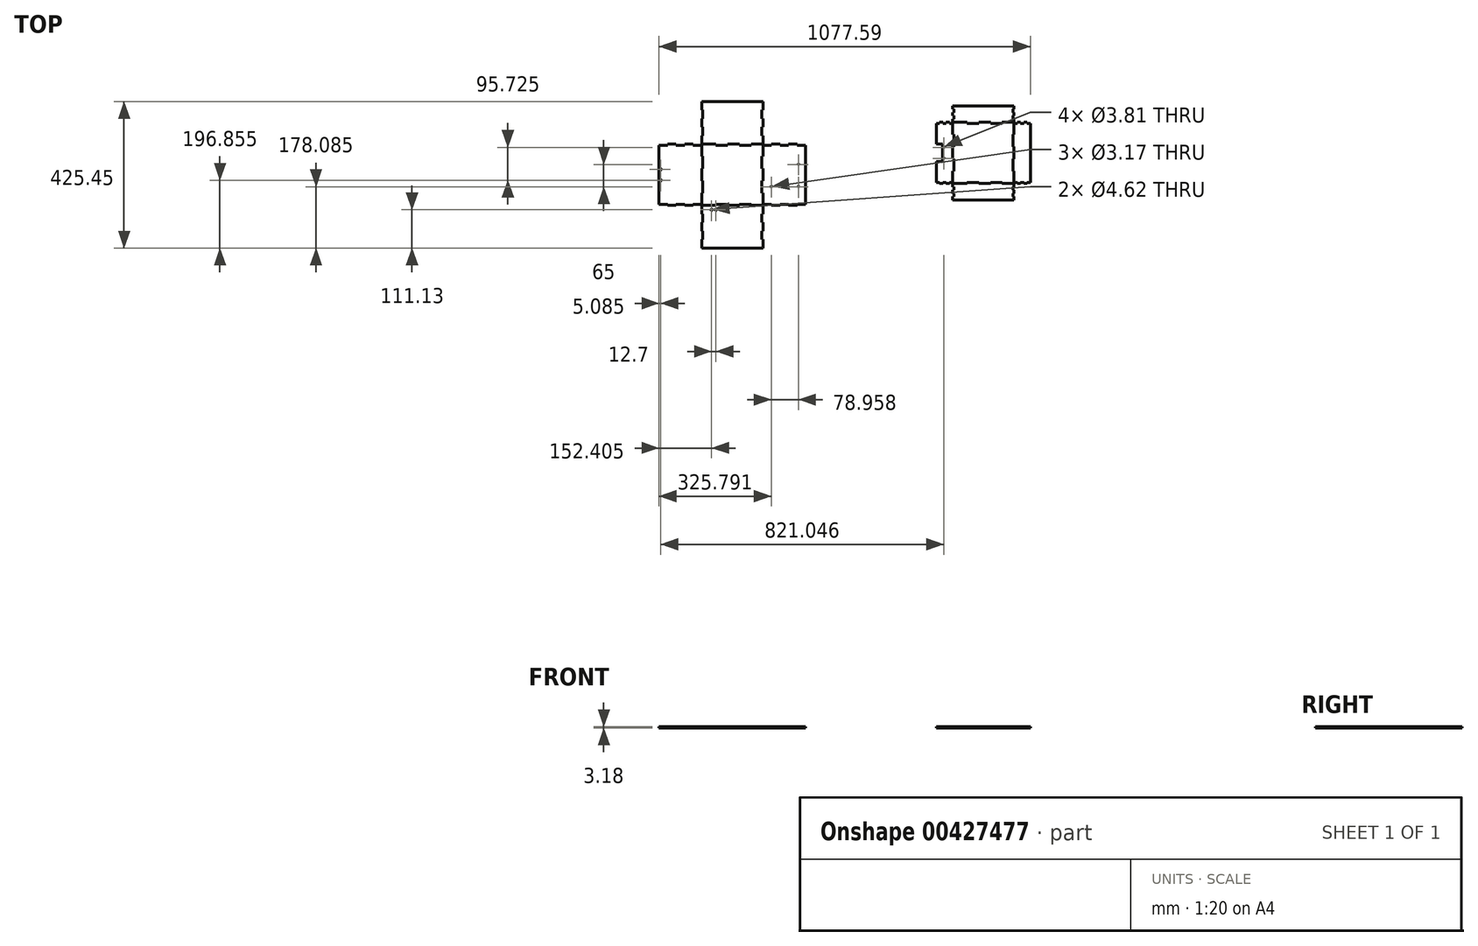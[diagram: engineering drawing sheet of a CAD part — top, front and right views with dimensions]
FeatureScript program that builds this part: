
annotation { "Feature Type Name" : "Feature", "Feature Type Description" : "" }
export const myFeature = defineFeature(function(context is Context, id is Id, definition is map)
    precondition{}
    {
        {
            var Q0;
            Q0=qCreatedBy(makeId("Top.planeOp"),FACE);
            var sketch = newSketch(context, id + "F0", { "sketchPlane" : qUnion([Q0])});
            skLineSegment(sketch, "E0.bottom", {"start": v(0, 0) * mm, "end": v(41.1, 0) * mm});
            skLineSegment(sketch, "E0.top", {"start": v(0, 177.8) * mm, "end": v(41.1, 177.8) * mm});
            skLineSegment(sketch, "E0.left", {"start": v(0, 0) * mm, "end": v(0, 35.56) * mm});
            skLineSegment(sketch, "E0.right", {"start": v(177.8, 0) * mm, "end": v(177.8, 35.56) * mm});
            skLineSegment(sketch, "E1", {"start": v(41.1, 177.8) * mm, "end": v(41.1, 174.62) * mm});
            skLineSegment(sketch, "E2", {"start": v(41.1, 174.62) * mm, "end": v(75.28, 174.62) * mm});
            skLineSegment(sketch, "E3", {"start": v(75.28, 174.62) * mm, "end": v(75.28, 177.8) * mm});
            skLineSegment(sketch, "E4", {"start": v(75.28, 177.8) * mm, "end": v(109.45, 177.8) * mm});
            skLineSegment(sketch, "E5", {"start": v(109.45, 177.8) * mm, "end": v(109.45, 174.62) * mm});
            skLineSegment(sketch, "E6", {"start": v(109.45, 174.62) * mm, "end": v(143.63, 174.62) * mm});
            skLineSegment(sketch, "E7", {"start": v(143.63, 174.62) * mm, "end": v(143.63, 177.8) * mm});
            skLineSegment(sketch, "E8", {"start": v(177.8, 142.24) * mm, "end": v(174.63, 142.24) * mm});
            skLineSegment(sketch, "E9", {"start": v(174.63, 142.24) * mm, "end": v(174.63, 106.68) * mm});
            skLineSegment(sketch, "E10", {"start": v(174.63, 106.68) * mm, "end": v(177.8, 106.68) * mm});
            skLineSegment(sketch, "E11", {"start": v(177.8, 71.12) * mm, "end": v(174.62, 71.12) * mm});
            skLineSegment(sketch, "E12", {"start": v(174.62, 71.12) * mm, "end": v(174.62, 35.56) * mm});
            skLineSegment(sketch, "E13", {"start": v(174.62, 35.56) * mm, "end": v(177.8, 35.56) * mm});
            skLineSegment(sketch, "E14", {"start": v(0, 142.24) * mm, "end": v(3.18, 142.24) * mm});
            skLineSegment(sketch, "E15", {"start": v(3.18, 142.24) * mm, "end": v(3.18, 106.68) * mm});
            skLineSegment(sketch, "E16", {"start": v(3.18, 106.68) * mm, "end": v(0, 106.68) * mm});
            skLineSegment(sketch, "E17", {"start": v(0, 71.12) * mm, "end": v(3.18, 71.12) * mm});
            skLineSegment(sketch, "E18", {"start": v(3.18, 71.12) * mm, "end": v(3.18, 35.56) * mm});
            skLineSegment(sketch, "E19", {"start": v(3.18, 35.56) * mm, "end": v(0, 35.56) * mm});
            skLineSegment(sketch, "E20", {"start": v(41.1, 0) * mm, "end": v(41.1, 3.18) * mm});
            skLineSegment(sketch, "E21", {"start": v(41.1, 3.18) * mm, "end": v(75.28, 3.18) * mm});
            skLineSegment(sketch, "E22", {"start": v(75.28, 3.18) * mm, "end": v(75.28, 0) * mm});
            skLineSegment(sketch, "E23", {"start": v(109.45, 0) * mm, "end": v(109.45, 3.18) * mm});
            skLineSegment(sketch, "E24", {"start": v(109.45, 3.18) * mm, "end": v(143.63, 3.18) * mm});
            skLineSegment(sketch, "E25", {"start": v(143.63, 3.18) * mm, "end": v(143.63, 0) * mm});
            skLineSegment(sketch, "E26.trimOffspring", {"start": v(0, 142.24) * mm, "end": v(0, 177.8) * mm});
            skLineSegment(sketch, "E27.trimOffspring", {"start": v(143.63, 177.8) * mm, "end": v(177.8, 177.8) * mm});
            skLineSegment(sketch, "E28.trimOffspring", {"start": v(177.8, 142.24) * mm, "end": v(177.8, 177.8) * mm});
            skLineSegment(sketch, "E29.trimOffspring", {"start": v(177.8, 71.12) * mm, "end": v(177.8, 106.68) * mm});
            skLineSegment(sketch, "E30.trimOffspring", {"start": v(143.63, 0) * mm, "end": v(177.8, 0) * mm});
            skLineSegment(sketch, "E31.trimOffspring", {"start": v(75.28, 0) * mm, "end": v(109.45, 0) * mm});
            skLineSegment(sketch, "E32.trimOffspring", {"start": v(0, 71.12) * mm, "end": v(0, 106.68) * mm});
            skLineSegment(sketch, "E33", {"start": v(-24.77, 0) * mm, "end": v(-49.53, 0) * mm});
            skLineSegment(sketch, "E34", {"start": v(-123.83, 3.17) * mm, "end": v(-123.83, 174.62) * mm});
            skLineSegment(sketch, "E35", {"start": v(-99.06, 177.8) * mm, "end": v(-74.3, 177.8) * mm});
            skLineSegment(sketch, "E36", {"start": v(0, 301.62) * mm, "end": v(177.8, 301.62) * mm});
            skLineSegment(sketch, "E37", {"start": v(177.8, 301.62) * mm, "end": v(177.8, 276.86) * mm});
            skLineSegment(sketch, "E38", {"start": v(0, 301.62) * mm, "end": v(0, 276.86) * mm});
            skLineSegment(sketch, "E39", {"start": v(202.57, 177.8) * mm, "end": v(227.33, 177.8) * mm});
            skLineSegment(sketch, "E40", {"start": v(301.63, 174.62) * mm, "end": v(301.63, 3.18) * mm});
            skLineSegment(sketch, "E41", {"start": v(276.86, 0) * mm, "end": v(252.1, 0) * mm});
            skLineSegment(sketch, "E42", {"start": v(177.8, 0) * mm, "end": v(177.8, -24.77) * mm});
            skLineSegment(sketch, "E43", {"start": v(177.8, -123.83) * mm, "end": v(0, -123.83) * mm});
            skLineSegment(sketch, "E44", {"start": v(0, -123.83) * mm, "end": v(0, -99.06) * mm});
            skLineSegment(sketch, "E45", {"start": v(0, 276.86) * mm, "end": v(3.18, 276.86) * mm});
            skLineSegment(sketch, "E46", {"start": v(3.18, 276.86) * mm, "end": v(3.18, 252.1) * mm});
            skLineSegment(sketch, "E47", {"start": v(3.18, 252.1) * mm, "end": v(0, 252.1) * mm});
            skLineSegment(sketch, "E48", {"start": v(0, 227.33) * mm, "end": v(3.18, 227.33) * mm});
            skLineSegment(sketch, "E49", {"start": v(3.18, 227.33) * mm, "end": v(3.18, 202.56) * mm});
            skLineSegment(sketch, "E50", {"start": v(3.18, 202.56) * mm, "end": v(0, 202.56) * mm});
            skLineSegment(sketch, "E51", {"start": v(177.8, 276.86) * mm, "end": v(174.62, 276.86) * mm});
            skLineSegment(sketch, "E52", {"start": v(174.62, 276.86) * mm, "end": v(174.62, 252.1) * mm});
            skLineSegment(sketch, "E53", {"start": v(174.62, 252.1) * mm, "end": v(177.8, 252.1) * mm});
            skLineSegment(sketch, "E54", {"start": v(177.8, 227.33) * mm, "end": v(174.62, 227.33) * mm});
            skLineSegment(sketch, "E55", {"start": v(174.62, 227.33) * mm, "end": v(174.62, 202.56) * mm});
            skLineSegment(sketch, "E56", {"start": v(174.62, 202.56) * mm, "end": v(177.8, 202.56) * mm});
            skLineSegment(sketch, "E57.trimOffspring", {"start": v(0, 252.1) * mm, "end": v(0, 227.33) * mm});
            skLineSegment(sketch, "E58.trimOffspring", {"start": v(0, 202.56) * mm, "end": v(0, 177.8) * mm});
            skLineSegment(sketch, "E59.trimOffspring", {"start": v(177.8, 252.1) * mm, "end": v(177.8, 227.33) * mm});
            skLineSegment(sketch, "E60.trimOffspring", {"start": v(177.8, 202.56) * mm, "end": v(177.8, 177.8) * mm});
            skLineSegment(sketch, "E61", {"start": v(0, -24.77) * mm, "end": v(3.18, -24.77) * mm});
            skLineSegment(sketch, "E62", {"start": v(3.18, -24.77) * mm, "end": v(3.18, -49.53) * mm});
            skLineSegment(sketch, "E63", {"start": v(3.18, -49.53) * mm, "end": v(0, -49.53) * mm});
            skLineSegment(sketch, "E64", {"start": v(0, -74.3) * mm, "end": v(3.18, -74.3) * mm});
            skLineSegment(sketch, "E65", {"start": v(3.18, -74.3) * mm, "end": v(3.18, -99.06) * mm});
            skLineSegment(sketch, "E66", {"start": v(3.18, -99.06) * mm, "end": v(0, -99.06) * mm});
            skLineSegment(sketch, "E67", {"start": v(177.8, -24.77) * mm, "end": v(174.63, -24.77) * mm});
            skLineSegment(sketch, "E68", {"start": v(174.63, -24.77) * mm, "end": v(174.63, -49.53) * mm});
            skLineSegment(sketch, "E69", {"start": v(174.63, -49.53) * mm, "end": v(177.8, -49.53) * mm});
            skLineSegment(sketch, "E70", {"start": v(177.8, -74.3) * mm, "end": v(174.63, -74.3) * mm});
            skLineSegment(sketch, "E71", {"start": v(174.63, -74.3) * mm, "end": v(174.63, -99.06) * mm});
            skLineSegment(sketch, "E72", {"start": v(174.63, -99.06) * mm, "end": v(177.8, -99.06) * mm});
            skLineSegment(sketch, "E73.trimOffspring", {"start": v(0, -24.77) * mm, "end": v(0, 0) * mm});
            skLineSegment(sketch, "E74.trimOffspring", {"start": v(0, -74.3) * mm, "end": v(0, -49.53) * mm});
            skLineSegment(sketch, "E75.trimOffspring", {"start": v(177.8, -49.53) * mm, "end": v(177.8, -74.3) * mm});
            skLineSegment(sketch, "E76.trimOffspring", {"start": v(177.8, -99.06) * mm, "end": v(177.8, -123.83) * mm});
            skLineSegment(sketch, "E77", {"start": v(177.8, 174.62) * mm, "end": v(202.57, 174.62) * mm});
            skLineSegment(sketch, "E78", {"start": v(202.57, 174.62) * mm, "end": v(202.57, 177.8) * mm});
            skLineSegment(sketch, "E79", {"start": v(227.33, 177.8) * mm, "end": v(227.33, 174.62) * mm});
            skLineSegment(sketch, "E80", {"start": v(227.33, 174.62) * mm, "end": v(252.1, 174.62) * mm});
            skLineSegment(sketch, "E81", {"start": v(252.1, 174.63) * mm, "end": v(252.1, 177.8) * mm});
            skLineSegment(sketch, "E82", {"start": v(276.86, 177.8) * mm, "end": v(276.86, 174.62) * mm});
            skLineSegment(sketch, "E83", {"start": v(276.86, 174.62) * mm, "end": v(301.62, 174.62) * mm});
            skLineSegment(sketch, "E84", {"start": v(177.8, 3.18) * mm, "end": v(202.57, 3.18) * mm});
            skLineSegment(sketch, "E85", {"start": v(202.57, 3.18) * mm, "end": v(202.57, 0) * mm});
            skLineSegment(sketch, "E86", {"start": v(276.86, 0) * mm, "end": v(276.86, 3.18) * mm});
            skLineSegment(sketch, "E87", {"start": v(276.86, 3.18) * mm, "end": v(301.63, 3.18) * mm});
            skLineSegment(sketch, "E88", {"start": v(227.33, 0) * mm, "end": v(227.33, 3.18) * mm});
            skLineSegment(sketch, "E89", {"start": v(227.33, 3.18) * mm, "end": v(252.1, 3.18) * mm});
            skLineSegment(sketch, "E90", {"start": v(252.1, 3.18) * mm, "end": v(252.1, 0) * mm});
            skLineSegment(sketch, "E91.trimOffspring", {"start": v(252.1, 177.8) * mm, "end": v(276.86, 177.8) * mm});
            skPoint(sketch, "E92.orphan", {"position": v(301.63, 0) * mm});
            skLineSegment(sketch, "E93.trimOffspring", {"start": v(227.33, 0) * mm, "end": v(202.57, 0) * mm});
            skLineSegment(sketch, "E94", {"start": v(0, 174.62) * mm, "end": v(-24.77, 174.62) * mm});
            skLineSegment(sketch, "E95", {"start": v(-24.77, 174.62) * mm, "end": v(-24.77, 177.8) * mm});
            skLineSegment(sketch, "E96", {"start": v(-123.83, 174.62) * mm, "end": v(-99.06, 174.62) * mm});
            skLineSegment(sketch, "E97", {"start": v(-99.06, 174.62) * mm, "end": v(-99.06, 177.8) * mm});
            skLineSegment(sketch, "E98", {"start": v(-74.3, 177.8) * mm, "end": v(-74.3, 174.62) * mm});
            skLineSegment(sketch, "E99", {"start": v(-74.3, 174.62) * mm, "end": v(-49.53, 174.62) * mm});
            skLineSegment(sketch, "E100", {"start": v(-49.53, 174.62) * mm, "end": v(-49.53, 177.8) * mm});
            skLineSegment(sketch, "E101", {"start": v(0, 3.18) * mm, "end": v(-24.77, 3.18) * mm});
            skLineSegment(sketch, "E102", {"start": v(-24.77, 3.18) * mm, "end": v(-24.77, 0) * mm});
            skLineSegment(sketch, "E103", {"start": v(-99.06, 0) * mm, "end": v(-99.06, 3.18) * mm});
            skLineSegment(sketch, "E104", {"start": v(-99.06, 3.18) * mm, "end": v(-123.83, 3.18) * mm});
            skLineSegment(sketch, "E105", {"start": v(-74.3, 0) * mm, "end": v(-74.3, 3.18) * mm});
            skLineSegment(sketch, "E106", {"start": v(-74.3, 3.18) * mm, "end": v(-49.53, 3.18) * mm});
            skLineSegment(sketch, "E107", {"start": v(-49.53, 3.18) * mm, "end": v(-49.53, 0) * mm});
            skLineSegment(sketch, "E108.trimOffspring", {"start": v(-49.53, 177.8) * mm, "end": v(-24.77, 177.8) * mm});
            skLineSegment(sketch, "E109.trimOffspring", {"start": v(-74.3, 0) * mm, "end": v(-99.06, 0) * mm});
            skLineSegment(sketch, "E110.bottom", {"start": v(728.34, 63.97) * mm, "end": v(769.44, 63.97) * mm});
            skLineSegment(sketch, "E110.top", {"start": v(728.34, 241.77) * mm, "end": v(769.44, 241.77) * mm});
            skLineSegment(sketch, "E110.left", {"start": v(728.34, 63.97) * mm, "end": v(728.34, 99.53) * mm});
            skLineSegment(sketch, "E110.right", {"start": v(906.14, 63.97) * mm, "end": v(906.14, 99.53) * mm});
            skLineSegment(sketch, "E111", {"start": v(769.44, 241.77) * mm, "end": v(769.44, 238.6) * mm});
            skLineSegment(sketch, "E112", {"start": v(769.44, 238.6) * mm, "end": v(803.61, 238.6) * mm});
            skLineSegment(sketch, "E113", {"start": v(803.61, 238.6) * mm, "end": v(803.61, 241.77) * mm});
            skLineSegment(sketch, "E114", {"start": v(803.61, 241.77) * mm, "end": v(837.79, 241.77) * mm});
            skLineSegment(sketch, "E115", {"start": v(837.79, 241.77) * mm, "end": v(837.79, 238.6) * mm});
            skLineSegment(sketch, "E116", {"start": v(837.79, 238.6) * mm, "end": v(871.96, 238.6) * mm});
            skLineSegment(sketch, "E117", {"start": v(871.96, 238.6) * mm, "end": v(871.96, 241.77) * mm});
            skLineSegment(sketch, "E118", {"start": v(906.14, 206.21) * mm, "end": v(902.96, 206.21) * mm});
            skLineSegment(sketch, "E119", {"start": v(902.96, 206.21) * mm, "end": v(902.96, 170.65) * mm});
            skLineSegment(sketch, "E120", {"start": v(902.96, 170.65) * mm, "end": v(906.14, 170.65) * mm});
            skLineSegment(sketch, "E121", {"start": v(906.14, 135.1) * mm, "end": v(902.96, 135.1) * mm});
            skLineSegment(sketch, "E122", {"start": v(902.96, 135.1) * mm, "end": v(902.96, 99.53) * mm});
            skLineSegment(sketch, "E123", {"start": v(902.96, 99.53) * mm, "end": v(906.14, 99.53) * mm});
            skLineSegment(sketch, "E124", {"start": v(728.34, 206.21) * mm, "end": v(731.51, 206.21) * mm});
            skLineSegment(sketch, "E125", {"start": v(731.51, 206.21) * mm, "end": v(731.51, 170.65) * mm});
            skLineSegment(sketch, "E126", {"start": v(731.51, 170.65) * mm, "end": v(728.34, 170.65) * mm});
            skLineSegment(sketch, "E127", {"start": v(728.34, 135.1) * mm, "end": v(731.51, 135.1) * mm});
            skLineSegment(sketch, "E128", {"start": v(731.51, 135.1) * mm, "end": v(731.51, 99.53) * mm});
            skLineSegment(sketch, "E129", {"start": v(731.51, 99.53) * mm, "end": v(728.34, 99.53) * mm});
            skLineSegment(sketch, "E130", {"start": v(769.44, 63.97) * mm, "end": v(769.44, 67.15) * mm});
            skLineSegment(sketch, "E131", {"start": v(769.44, 67.15) * mm, "end": v(803.61, 67.15) * mm});
            skLineSegment(sketch, "E132", {"start": v(803.61, 67.15) * mm, "end": v(803.61, 63.97) * mm});
            skLineSegment(sketch, "E133", {"start": v(837.79, 63.97) * mm, "end": v(837.79, 67.15) * mm});
            skLineSegment(sketch, "E134", {"start": v(837.79, 67.15) * mm, "end": v(871.96, 67.15) * mm});
            skLineSegment(sketch, "E135", {"start": v(871.96, 67.15) * mm, "end": v(871.96, 63.97) * mm});
            skLineSegment(sketch, "E136.trimOffspring", {"start": v(728.34, 206.21) * mm, "end": v(728.34, 241.77) * mm});
            skLineSegment(sketch, "E137.trimOffspring", {"start": v(871.96, 241.77) * mm, "end": v(906.14, 241.77) * mm});
            skLineSegment(sketch, "E138.trimOffspring", {"start": v(906.14, 206.21) * mm, "end": v(906.14, 241.77) * mm});
            skLineSegment(sketch, "E139.trimOffspring", {"start": v(906.14, 135.1) * mm, "end": v(906.14, 170.65) * mm});
            skLineSegment(sketch, "E140.trimOffspring", {"start": v(871.96, 63.97) * mm, "end": v(906.14, 63.97) * mm});
            skLineSegment(sketch, "E141.trimOffspring", {"start": v(803.61, 63.97) * mm, "end": v(837.79, 63.97) * mm});
            skLineSegment(sketch, "E142.trimOffspring", {"start": v(728.34, 135.1) * mm, "end": v(728.34, 170.65) * mm});
            skLineSegment(sketch, "E143", {"start": v(718.81, 63.97) * mm, "end": v(709.29, 63.97) * mm});
            skLineSegment(sketch, "E144", {"start": v(680.71, 67.15) * mm, "end": v(680.71, 238.6) * mm});
            skLineSegment(sketch, "E145", {"start": v(690.24, 241.77) * mm, "end": v(699.76, 241.77) * mm});
            skLineSegment(sketch, "E146", {"start": v(728.34, 289.4) * mm, "end": v(906.14, 289.4) * mm});
            skLineSegment(sketch, "E147", {"start": v(906.14, 289.4) * mm, "end": v(906.14, 279.87) * mm});
            skLineSegment(sketch, "E148", {"start": v(728.34, 289.4) * mm, "end": v(728.34, 279.87) * mm});
            skLineSegment(sketch, "E149", {"start": v(915.66, 241.77) * mm, "end": v(925.19, 241.77) * mm});
            skLineSegment(sketch, "E150", {"start": v(953.76, 238.6) * mm, "end": v(953.76, 67.15) * mm});
            skLineSegment(sketch, "E151", {"start": v(944.24, 63.97) * mm, "end": v(934.71, 63.97) * mm});
            skLineSegment(sketch, "E152", {"start": v(906.14, 63.97) * mm, "end": v(906.14, 54.45) * mm});
            skLineSegment(sketch, "E153", {"start": v(906.14, 16.35) * mm, "end": v(728.34, 16.35) * mm});
            skLineSegment(sketch, "E154", {"start": v(728.34, 16.35) * mm, "end": v(728.34, 25.87) * mm});
            skLineSegment(sketch, "E155", {"start": v(728.34, 279.87) * mm, "end": v(731.51, 279.87) * mm});
            skLineSegment(sketch, "E156", {"start": v(731.51, 279.87) * mm, "end": v(731.51, 270.35) * mm});
            skLineSegment(sketch, "E157", {"start": v(731.51, 270.35) * mm, "end": v(728.34, 270.35) * mm});
            skLineSegment(sketch, "E158", {"start": v(728.34, 260.82) * mm, "end": v(731.51, 260.82) * mm});
            skLineSegment(sketch, "E159", {"start": v(731.51, 260.82) * mm, "end": v(731.51, 251.3) * mm});
            skLineSegment(sketch, "E160", {"start": v(731.51, 251.3) * mm, "end": v(728.34, 251.3) * mm});
            skLineSegment(sketch, "E161", {"start": v(906.14, 279.87) * mm, "end": v(902.96, 279.87) * mm});
            skLineSegment(sketch, "E162", {"start": v(902.96, 279.87) * mm, "end": v(902.96, 270.35) * mm});
            skLineSegment(sketch, "E163", {"start": v(902.96, 270.35) * mm, "end": v(906.14, 270.35) * mm});
            skLineSegment(sketch, "E164", {"start": v(906.14, 260.82) * mm, "end": v(902.96, 260.82) * mm});
            skLineSegment(sketch, "E165", {"start": v(902.96, 260.82) * mm, "end": v(902.96, 251.3) * mm});
            skLineSegment(sketch, "E166", {"start": v(902.96, 251.3) * mm, "end": v(906.14, 251.3) * mm});
            skLineSegment(sketch, "E167.trimOffspring", {"start": v(728.34, 270.35) * mm, "end": v(728.34, 260.82) * mm});
            skLineSegment(sketch, "E168.trimOffspring", {"start": v(728.34, 251.3) * mm, "end": v(728.34, 241.77) * mm});
            skLineSegment(sketch, "E169.trimOffspring", {"start": v(906.14, 270.35) * mm, "end": v(906.14, 260.82) * mm});
            skLineSegment(sketch, "E170.trimOffspring", {"start": v(906.14, 251.3) * mm, "end": v(906.14, 241.77) * mm});
            skLineSegment(sketch, "E171", {"start": v(728.34, 54.45) * mm, "end": v(731.51, 54.45) * mm});
            skLineSegment(sketch, "E172", {"start": v(731.51, 54.45) * mm, "end": v(731.51, 44.92) * mm});
            skLineSegment(sketch, "E173", {"start": v(731.51, 44.92) * mm, "end": v(728.34, 44.92) * mm});
            skLineSegment(sketch, "E174", {"start": v(728.34, 35.4) * mm, "end": v(731.51, 35.4) * mm});
            skLineSegment(sketch, "E175", {"start": v(731.51, 35.4) * mm, "end": v(731.51, 25.87) * mm});
            skLineSegment(sketch, "E176", {"start": v(731.51, 25.87) * mm, "end": v(728.34, 25.87) * mm});
            skLineSegment(sketch, "E177", {"start": v(906.14, 54.45) * mm, "end": v(902.96, 54.45) * mm});
            skLineSegment(sketch, "E178", {"start": v(902.96, 54.45) * mm, "end": v(902.96, 44.92) * mm});
            skLineSegment(sketch, "E179", {"start": v(902.96, 44.92) * mm, "end": v(906.14, 44.92) * mm});
            skLineSegment(sketch, "E180", {"start": v(906.14, 35.4) * mm, "end": v(902.96, 35.4) * mm});
            skLineSegment(sketch, "E181", {"start": v(902.96, 35.4) * mm, "end": v(902.96, 25.87) * mm});
            skLineSegment(sketch, "E182", {"start": v(902.96, 25.87) * mm, "end": v(906.14, 25.87) * mm});
            skLineSegment(sketch, "E183.trimOffspring", {"start": v(728.34, 54.45) * mm, "end": v(728.34, 63.97) * mm});
            skLineSegment(sketch, "E184.trimOffspring", {"start": v(728.34, 35.4) * mm, "end": v(728.34, 44.92) * mm});
            skLineSegment(sketch, "E185.trimOffspring", {"start": v(906.14, 44.92) * mm, "end": v(906.14, 35.4) * mm});
            skLineSegment(sketch, "E186.trimOffspring", {"start": v(906.14, 25.87) * mm, "end": v(906.14, 16.35) * mm});
            skLineSegment(sketch, "E187", {"start": v(906.14, 238.6) * mm, "end": v(915.66, 238.6) * mm});
            skLineSegment(sketch, "E188", {"start": v(915.66, 238.6) * mm, "end": v(915.66, 241.77) * mm});
            skLineSegment(sketch, "E189", {"start": v(925.19, 241.77) * mm, "end": v(925.19, 238.6) * mm});
            skLineSegment(sketch, "E190", {"start": v(925.19, 238.6) * mm, "end": v(934.71, 238.6) * mm});
            skLineSegment(sketch, "E191", {"start": v(934.71, 238.6) * mm, "end": v(934.71, 241.77) * mm});
            skLineSegment(sketch, "E192", {"start": v(944.24, 241.77) * mm, "end": v(944.24, 238.6) * mm});
            skLineSegment(sketch, "E193", {"start": v(944.24, 238.6) * mm, "end": v(953.76, 238.6) * mm});
            skLineSegment(sketch, "E194", {"start": v(906.14, 67.15) * mm, "end": v(915.66, 67.15) * mm});
            skLineSegment(sketch, "E195", {"start": v(915.66, 67.15) * mm, "end": v(915.66, 63.97) * mm});
            skLineSegment(sketch, "E196", {"start": v(944.24, 63.97) * mm, "end": v(944.24, 67.15) * mm});
            skLineSegment(sketch, "E197", {"start": v(944.24, 67.15) * mm, "end": v(953.76, 67.15) * mm});
            skLineSegment(sketch, "E198", {"start": v(925.19, 63.97) * mm, "end": v(925.19, 67.15) * mm});
            skLineSegment(sketch, "E199", {"start": v(925.19, 67.15) * mm, "end": v(934.71, 67.15) * mm});
            skLineSegment(sketch, "E200", {"start": v(934.71, 67.15) * mm, "end": v(934.71, 63.97) * mm});
            skLineSegment(sketch, "E201.trimOffspring", {"start": v(934.71, 241.77) * mm, "end": v(944.24, 241.77) * mm});
            skPoint(sketch, "E202.orphan", {"position": v(953.76, 63.97) * mm});
            skLineSegment(sketch, "E203.trimOffspring", {"start": v(925.19, 63.97) * mm, "end": v(915.66, 63.97) * mm});
            skLineSegment(sketch, "E204", {"start": v(728.34, 238.6) * mm, "end": v(718.81, 238.6) * mm});
            skLineSegment(sketch, "E205", {"start": v(718.81, 238.6) * mm, "end": v(718.81, 241.77) * mm});
            skLineSegment(sketch, "E206", {"start": v(680.71, 238.6) * mm, "end": v(690.24, 238.6) * mm});
            skLineSegment(sketch, "E207", {"start": v(690.24, 238.6) * mm, "end": v(690.24, 241.77) * mm});
            skLineSegment(sketch, "E208", {"start": v(699.76, 241.77) * mm, "end": v(699.76, 238.6) * mm});
            skLineSegment(sketch, "E209", {"start": v(699.76, 238.6) * mm, "end": v(709.29, 238.6) * mm});
            skLineSegment(sketch, "E210", {"start": v(709.29, 238.6) * mm, "end": v(709.29, 241.77) * mm});
            skLineSegment(sketch, "E211", {"start": v(728.34, 67.15) * mm, "end": v(718.81, 67.15) * mm});
            skLineSegment(sketch, "E212", {"start": v(718.81, 67.15) * mm, "end": v(718.81, 63.97) * mm});
            skLineSegment(sketch, "E213", {"start": v(690.24, 63.97) * mm, "end": v(690.24, 67.15) * mm});
            skLineSegment(sketch, "E214", {"start": v(690.24, 67.15) * mm, "end": v(680.71, 67.15) * mm});
            skLineSegment(sketch, "E215", {"start": v(699.76, 63.97) * mm, "end": v(699.76, 67.15) * mm});
            skLineSegment(sketch, "E216", {"start": v(699.76, 67.15) * mm, "end": v(709.29, 67.15) * mm});
            skLineSegment(sketch, "E217", {"start": v(709.29, 67.15) * mm, "end": v(709.29, 63.97) * mm});
            skLineSegment(sketch, "E218.trimOffspring", {"start": v(709.29, 241.77) * mm, "end": v(718.81, 241.77) * mm});
            skLineSegment(sketch, "E219.trimOffspring", {"start": v(699.76, 63.97) * mm, "end": v(690.24, 63.97) * mm});
            skSolve(sketch);
        }
        {
            var Q0;
            {var subQ6=sQuery(id+"F0.wireOp",EDGE,"E0.bottom");Q0=makeQuery(id+"F0.imprint","IMPRINT",FACE,{"disambiguationData":[TD([[makeQuery(id+"F0.imprint","IMPRINT",EDGE,{"derivedFrom":subQ6}),1.0]])]});}
            extrude(context, id + "F1", {"entities" : qUnion([Q0]), "depth" : 3.17 * mm});
        }
        {
            var Q0;
            Q0=makeQuery(id+"F0.imprint","IMPRINT",FACE,{"disambiguationData":[TD([[makeQuery(id+"F0.imprint","IMPRINT",EDGE,{"derivedFrom":sQuery(id+"F0.wireOp",EDGE,"E0.top")}),1.0]])]});
            extrude(context, id + "F2", {"entities" : qUnion([Q0]), "depth" : 3.17 * mm});
        }
        {
            var Q0;
            {var subQ3=sQuery(id+"F0.wireOp",EDGE,"E14");Q0=makeQuery(id+"F0.imprint","IMPRINT",FACE,{"disambiguationData":[TD([[makeQuery(id+"F0.imprint","IMPRINT",EDGE,{"derivedFrom":subQ3}),-1.0]])]});}
            extrude(context, id + "F3", {"entities" : qUnion([Q0]), "depth" : 3.17 * mm});
        }
        {
            var Q0;
            {var subQ1=sQuery(id+"F0.wireOp",EDGE,"E8");Q0=makeQuery(id+"F0.imprint","IMPRINT",FACE,{"disambiguationData":[TD([[makeQuery(id+"F0.imprint","IMPRINT",EDGE,{"derivedFrom":subQ1}),1.0]])]});}
            extrude(context, id + "F4", {"entities" : qUnion([Q0]), "depth" : 3.17 * mm});
        }
        {
            var Q0;
            Q0=makeQuery(id+"F0.imprint","IMPRINT",FACE,{"disambiguationData":[TD([[makeQuery(id+"F0.imprint","IMPRINT",EDGE,{"derivedFrom":sQuery(id+"F0.wireOp",EDGE,"E0.bottom")}),-1.0]])]});
            extrude(context, id + "F5", {"entities" : qUnion([Q0]), "depth" : 3.17 * mm});
        }
        {
            var Q0;
            Q0=makeQuery(id+"F5.opExtrude","CAP_FACE",FACE,{"disambiguationData":[OSD([sQuery(id+"F0.wireOp",EDGE,"E0.bottom"),sQuery(id+"F0.wireOp",EDGE,"E20"),sQuery(id+"F0.wireOp",EDGE,"E21"),sQuery(id+"F0.wireOp",EDGE,"E22"),sQuery(id+"F0.wireOp",EDGE,"E23"),sQuery(id+"F0.wireOp",EDGE,"E24"),sQuery(id+"F0.wireOp",EDGE,"E25"),sQuery(id+"F0.wireOp",EDGE,"E30.trimOffspring"),sQuery(id+"F0.wireOp",EDGE,"E31.trimOffspring"),sQuery(id+"F0.wireOp",EDGE,"E42"),sQuery(id+"F0.wireOp",EDGE,"E43"),sQuery(id+"F0.wireOp",EDGE,"E44"),sQuery(id+"F0.wireOp",EDGE,"E61"),sQuery(id+"F0.wireOp",EDGE,"E62"),sQuery(id+"F0.wireOp",EDGE,"E63"),sQuery(id+"F0.wireOp",EDGE,"E64"),sQuery(id+"F0.wireOp",EDGE,"E65"),sQuery(id+"F0.wireOp",EDGE,"E66"),sQuery(id+"F0.wireOp",EDGE,"E67"),sQuery(id+"F0.wireOp",EDGE,"E68"),sQuery(id+"F0.wireOp",EDGE,"E69"),sQuery(id+"F0.wireOp",EDGE,"E70"),sQuery(id+"F0.wireOp",EDGE,"E71"),sQuery(id+"F0.wireOp",EDGE,"E72"),sQuery(id+"F0.wireOp",EDGE,"E73.trimOffspring"),sQuery(id+"F0.wireOp",EDGE,"E74.trimOffspring"),sQuery(id+"F0.wireOp",EDGE,"E75.trimOffspring"),sQuery(id+"F0.wireOp",EDGE,"E76.trimOffspring")])],"isStart":false});
            var sketch = newSketch(context, id + "F6", { "sketchPlane" : qUnion([Q0])});
            skCircle(sketch, "E220", {"center": v(28.57, -12.7) * mm, "radius": 2.31 * mm});
            skCircle(sketch, "E221", {"center": v(41.28, -12.7) * mm, "radius": 2.31 * mm});
            skLineSegment(sketch, "E222.bottom", {"start": v(441.77, 26.41) * mm, "end": v(532.02, 26.41) * mm});
            skLineSegment(sketch, "E222.top", {"start": v(441.77, -58.39) * mm, "end": v(532.02, -58.39) * mm});
            skLineSegment(sketch, "E222.left", {"start": v(441.77, 26.41) * mm, "end": v(441.77, -58.39) * mm});
            skLineSegment(sketch, "E222.right", {"start": v(532.02, 26.41) * mm, "end": v(532.02, -58.39) * mm});
            skPoint(sketch, "E223", {"position": v(486.9, 26.41) * mm});
            skCircle(sketch, "E224", {"center": v(526.82, 14.37) * mm, "radius": 1.59 * mm});
            skCircle(sketch, "E225", {"center": v(526.82, -50.63) * mm, "radius": 1.59 * mm});
            skPoint(sketch, "E226", {"position": v(532.02, -15.99) * mm});
            skCircle(sketch, "E227", {"center": v(447.86, -50.5) * mm, "radius": 1.59 * mm});
            skSolve(sketch);
        }
        {
            var Q0;
            Q0=makeQuery(id+"F6.imprint","IMPRINT",FACE,{"disambiguationData":[TD([[makeQuery(id+"F6.imprint","IMPRINT",EDGE,{"derivedFrom":sQuery(id+"F6.wireOp",EDGE,"E220")}),1.0]])]});
            var Q1;
            Q1=makeQuery(id+"F6.imprint","IMPRINT",FACE,{"disambiguationData":[TD([[makeQuery(id+"F6.imprint","IMPRINT",EDGE,{"derivedFrom":sQuery(id+"F6.wireOp",EDGE,"E221")}),1.0]])]});
            extrude(context, id + "F7", {"entities" : qUnion([Q0, Q1]), "operationType" : NewBodyOperationType.REMOVE, "oppositeDirection" : true, "depth" : 25.4 * mm});
        }
        {
            var Q0;
            Q0=makeQuery(id+"F4.opExtrude","CAP_FACE",FACE,{"disambiguationData":[OSD([sQuery(id+"F0.wireOp",EDGE,"E0.right"),sQuery(id+"F0.wireOp",EDGE,"E8"),sQuery(id+"F0.wireOp",EDGE,"E9"),sQuery(id+"F0.wireOp",EDGE,"E10"),sQuery(id+"F0.wireOp",EDGE,"E11"),sQuery(id+"F0.wireOp",EDGE,"E12"),sQuery(id+"F0.wireOp",EDGE,"E13"),sQuery(id+"F0.wireOp",EDGE,"E28.trimOffspring"),sQuery(id+"F0.wireOp",EDGE,"E29.trimOffspring"),sQuery(id+"F0.wireOp",EDGE,"E39"),sQuery(id+"F0.wireOp",EDGE,"E40"),sQuery(id+"F0.wireOp",EDGE,"E41"),sQuery(id+"F0.wireOp",EDGE,"E77"),sQuery(id+"F0.wireOp",EDGE,"E78"),sQuery(id+"F0.wireOp",EDGE,"E79"),sQuery(id+"F0.wireOp",EDGE,"E80"),sQuery(id+"F0.wireOp",EDGE,"E81"),sQuery(id+"F0.wireOp",EDGE,"E82"),sQuery(id+"F0.wireOp",EDGE,"E83"),sQuery(id+"F0.wireOp",EDGE,"E84"),sQuery(id+"F0.wireOp",EDGE,"E85"),sQuery(id+"F0.wireOp",EDGE,"E86"),sQuery(id+"F0.wireOp",EDGE,"E87"),sQuery(id+"F0.wireOp",EDGE,"E88"),sQuery(id+"F0.wireOp",EDGE,"E89"),sQuery(id+"F0.wireOp",EDGE,"E90"),sQuery(id+"F0.wireOp",EDGE,"E91.trimOffspring"),sQuery(id+"F0.wireOp",EDGE,"E93.trimOffspring")])],"isStart":false});
            var sketch = newSketch(context, id + "F8", { "sketchPlane" : qUnion([Q0])});
            skLineSegment(sketch, "E228.bottom", {"start": v(195.87, 131.3) * mm, "end": v(286.12, 131.3) * mm});
            skLineSegment(sketch, "E228.top", {"start": v(195.87, 46.5) * mm, "end": v(286.12, 46.5) * mm});
            skLineSegment(sketch, "E228.left", {"start": v(195.87, 131.3) * mm, "end": v(195.87, 46.5) * mm});
            skLineSegment(sketch, "E228.right", {"start": v(286.12, 131.3) * mm, "end": v(286.12, 46.5) * mm});
            skPoint(sketch, "E229", {"position": v(241, 131.3) * mm});
            skCircle(sketch, "E230", {"center": v(280.92, 119.25) * mm, "radius": 1.59 * mm});
            skCircle(sketch, "E231", {"center": v(280.92, 54.25) * mm, "radius": 1.59 * mm});
            skPoint(sketch, "E232", {"position": v(286.12, 88.9) * mm});
            skCircle(sketch, "E233", {"center": v(201.96, 54.39) * mm, "radius": 1.59 * mm});
            skPoint(sketch, "E234", {"position": v(301.63, 88.9) * mm});
            skPoint(sketch, "E235", {"position": v(239.71, 174.62) * mm});
            skSolve(sketch);
        }
        {
            var Q0;
            Q0=makeQuery(id+"F8.imprint","IMPRINT",FACE,{"disambiguationData":[TD([[makeQuery(id+"F8.imprint","IMPRINT",EDGE,{"derivedFrom":sQuery(id+"F8.wireOp",EDGE,"E233")}),1.0]])]});
            var Q1;
            Q1=makeQuery(id+"F8.imprint","IMPRINT",FACE,{"disambiguationData":[TD([[makeQuery(id+"F8.imprint","IMPRINT",EDGE,{"derivedFrom":sQuery(id+"F8.wireOp",EDGE,"E231")}),1.0]])]});
            var Q2;
            Q2=makeQuery(id+"F8.imprint","IMPRINT",FACE,{"disambiguationData":[TD([[makeQuery(id+"F8.imprint","IMPRINT",EDGE,{"derivedFrom":sQuery(id+"F8.wireOp",EDGE,"E230")}),1.0]])]});
            extrude(context, id + "F9", {"entities" : qUnion([Q0, Q1, Q2]), "operationType" : NewBodyOperationType.REMOVE, "oppositeDirection" : true, "depth" : 25.4 * mm});
        }
        {
            var Q0;
            Q0=makeQuery(id+"F3.opExtrude","CAP_FACE",FACE,{"disambiguationData":[OSD([sQuery(id+"F0.wireOp",EDGE,"E0.left"),sQuery(id+"F0.wireOp",EDGE,"E14"),sQuery(id+"F0.wireOp",EDGE,"E15"),sQuery(id+"F0.wireOp",EDGE,"E16"),sQuery(id+"F0.wireOp",EDGE,"E17"),sQuery(id+"F0.wireOp",EDGE,"E18"),sQuery(id+"F0.wireOp",EDGE,"E19"),sQuery(id+"F0.wireOp",EDGE,"E26.trimOffspring"),sQuery(id+"F0.wireOp",EDGE,"E32.trimOffspring"),sQuery(id+"F0.wireOp",EDGE,"E33"),sQuery(id+"F0.wireOp",EDGE,"E34"),sQuery(id+"F0.wireOp",EDGE,"E35"),sQuery(id+"F0.wireOp",EDGE,"E94"),sQuery(id+"F0.wireOp",EDGE,"E95"),sQuery(id+"F0.wireOp",EDGE,"E96"),sQuery(id+"F0.wireOp",EDGE,"E97"),sQuery(id+"F0.wireOp",EDGE,"E98"),sQuery(id+"F0.wireOp",EDGE,"E99"),sQuery(id+"F0.wireOp",EDGE,"E100"),sQuery(id+"F0.wireOp",EDGE,"E101"),sQuery(id+"F0.wireOp",EDGE,"E102"),sQuery(id+"F0.wireOp",EDGE,"E103"),sQuery(id+"F0.wireOp",EDGE,"E104"),sQuery(id+"F0.wireOp",EDGE,"E105"),sQuery(id+"F0.wireOp",EDGE,"E106"),sQuery(id+"F0.wireOp",EDGE,"E107"),sQuery(id+"F0.wireOp",EDGE,"E108.trimOffspring"),sQuery(id+"F0.wireOp",EDGE,"E109.trimOffspring")])],"isStart":false});
            var sketch = newSketch(context, id + "F10", { "sketchPlane" : qUnion([Q0])});
            skCircle(sketch, "E236", {"center": v(-118.75, 104.78) * mm, "radius": 1.9 * mm});
            skCircle(sketch, "E237", {"center": v(-118.75, 73.03) * mm, "radius": 1.9 * mm});
            skSolve(sketch);
        }
        {
            var Q0;
            Q0=makeQuery(id+"F10.imprint","IMPRINT",FACE,{"disambiguationData":[TD([[makeQuery(id+"F10.imprint","IMPRINT",EDGE,{"derivedFrom":sQuery(id+"F10.wireOp",EDGE,"E236")}),1.0]])]});
            var Q1;
            Q1=makeQuery(id+"F10.imprint","IMPRINT",FACE,{"disambiguationData":[TD([[makeQuery(id+"F10.imprint","IMPRINT",EDGE,{"derivedFrom":sQuery(id+"F10.wireOp",EDGE,"E237")}),1.0]])]});
            extrude(context, id + "F11", {"entities" : qUnion([Q0, Q1]), "operationType" : NewBodyOperationType.REMOVE, "oppositeDirection" : true, "depth" : 25.4 * mm});
        }
        {
            var Q0;
            {var subQ6=sQuery(id+"F0.wireOp",EDGE,"E110.bottom");Q0=makeQuery(id+"F0.imprint","IMPRINT",FACE,{"disambiguationData":[TD([[makeQuery(id+"F0.imprint","IMPRINT",EDGE,{"derivedFrom":subQ6}),1.0]])]});}
            extrude(context, id + "F12", {"entities" : qUnion([Q0]), "depth" : 3.17 * mm});
        }
        {
            var Q0;
            {var subQ3=sQuery(id+"F0.wireOp",EDGE,"E124");Q0=makeQuery(id+"F0.imprint","IMPRINT",FACE,{"disambiguationData":[TD([[makeQuery(id+"F0.imprint","IMPRINT",EDGE,{"derivedFrom":subQ3}),-1.0]])]});}
            extrude(context, id + "F13", {"entities" : qUnion([Q0]), "depth" : 3.17 * mm});
        }
        {
            var Q0;
            Q0=makeQuery(id+"F0.imprint","IMPRINT",FACE,{"disambiguationData":[TD([[makeQuery(id+"F0.imprint","IMPRINT",EDGE,{"derivedFrom":sQuery(id+"F0.wireOp",EDGE,"E110.bottom")}),-1.0]])]});
            extrude(context, id + "F14", {"entities" : qUnion([Q0]), "depth" : 3.17 * mm});
        }
        {
            var Q0;
            Q0=makeQuery(id+"F0.imprint","IMPRINT",FACE,{"disambiguationData":[TD([[makeQuery(id+"F0.imprint","IMPRINT",EDGE,{"derivedFrom":sQuery(id+"F0.wireOp",EDGE,"E110.top")}),1.0]])]});
            extrude(context, id + "F15", {"entities" : qUnion([Q0]), "depth" : 3.17 * mm});
        }
        {
            var Q0;
            {var subQ1=sQuery(id+"F0.wireOp",EDGE,"E118");Q0=makeQuery(id+"F0.imprint","IMPRINT",FACE,{"disambiguationData":[TD([[makeQuery(id+"F0.imprint","IMPRINT",EDGE,{"derivedFrom":subQ1}),1.0]])]});}
            extrude(context, id + "F16", {"entities" : qUnion([Q0]), "depth" : 3.17 * mm});
        }
        {
            var Q0;
            Q0=makeQuery(id+"F13.opExtrude","CAP_FACE",FACE,{"disambiguationData":[OSD([sQuery(id+"F0.wireOp",EDGE,"E110.left"),sQuery(id+"F0.wireOp",EDGE,"E124"),sQuery(id+"F0.wireOp",EDGE,"E125"),sQuery(id+"F0.wireOp",EDGE,"E126"),sQuery(id+"F0.wireOp",EDGE,"E127"),sQuery(id+"F0.wireOp",EDGE,"E128"),sQuery(id+"F0.wireOp",EDGE,"E129"),sQuery(id+"F0.wireOp",EDGE,"E136.trimOffspring"),sQuery(id+"F0.wireOp",EDGE,"E142.trimOffspring"),sQuery(id+"F0.wireOp",EDGE,"E143"),sQuery(id+"F0.wireOp",EDGE,"E144"),sQuery(id+"F0.wireOp",EDGE,"E145"),sQuery(id+"F0.wireOp",EDGE,"E204"),sQuery(id+"F0.wireOp",EDGE,"E205"),sQuery(id+"F0.wireOp",EDGE,"E206"),sQuery(id+"F0.wireOp",EDGE,"E207"),sQuery(id+"F0.wireOp",EDGE,"E208"),sQuery(id+"F0.wireOp",EDGE,"E209"),sQuery(id+"F0.wireOp",EDGE,"E210"),sQuery(id+"F0.wireOp",EDGE,"E211"),sQuery(id+"F0.wireOp",EDGE,"E212"),sQuery(id+"F0.wireOp",EDGE,"E213"),sQuery(id+"F0.wireOp",EDGE,"E214"),sQuery(id+"F0.wireOp",EDGE,"E215"),sQuery(id+"F0.wireOp",EDGE,"E216"),sQuery(id+"F0.wireOp",EDGE,"E217"),sQuery(id+"F0.wireOp",EDGE,"E218.trimOffspring"),sQuery(id+"F0.wireOp",EDGE,"E219.trimOffspring")])],"isStart":false});
            var sketch = newSketch(context, id + "F17", { "sketchPlane" : qUnion([Q0])});
            skLineSegment(sketch, "E238.bottom", {"start": v(680.71, 178.27) * mm, "end": v(698.5, 178.27) * mm});
            skLineSegment(sketch, "E238.top", {"start": v(680.71, 127.47) * mm, "end": v(698.5, 127.47) * mm});
            skLineSegment(sketch, "E238.right", {"start": v(698.5, 178.27) * mm, "end": v(698.5, 127.47) * mm});
            skLineSegment(sketch, "E239", {"start": v(680.71, 178.27) * mm, "end": v(680.71, 127.47) * mm});
            skPoint(sketch, "E240", {"position": v(698.5, 152.87) * mm});
            skPoint(sketch, "E241", {"position": v(728.34, 152.87) * mm});
            skCircle(sketch, "E242", {"center": v(702.3, 168.75) * mm, "radius": 1.9 * mm});
            skCircle(sketch, "E243", {"center": v(702.3, 137) * mm, "radius": 1.9 * mm});
            skLineSegment(sketch, "E244", {"start": v(698.5, 178.27) * mm, "end": v(698.5, 152.87) * mm});
            skSolve(sketch);
        }
        {
            var Q0;
            Q0=makeQuery(id+"F17.imprint","IMPRINT",FACE,{"disambiguationData":[TD([[makeQuery(id+"F17.imprint","IMPRINT",EDGE,{"derivedFrom":sQuery(id+"F17.wireOp",EDGE,"E238.bottom")}),-1.0]])]});
            var Q1;
            Q1=makeQuery(id+"F17.imprint","IMPRINT",FACE,{"disambiguationData":[TD([[makeQuery(id+"F17.imprint","IMPRINT",EDGE,{"derivedFrom":sQuery(id+"F17.wireOp",EDGE,"E242")}),1.0]])]});
            var Q2;
            Q2=makeQuery(id+"F17.imprint","IMPRINT",FACE,{"disambiguationData":[TD([[makeQuery(id+"F17.imprint","IMPRINT",EDGE,{"derivedFrom":sQuery(id+"F17.wireOp",EDGE,"E243")}),1.0]])]});
            extrude(context, id + "F18", {"entities" : qUnion([Q0, Q1, Q2]), "operationType" : NewBodyOperationType.REMOVE, "oppositeDirection" : true, "depth" : 25.4 * mm});
        }
    });
